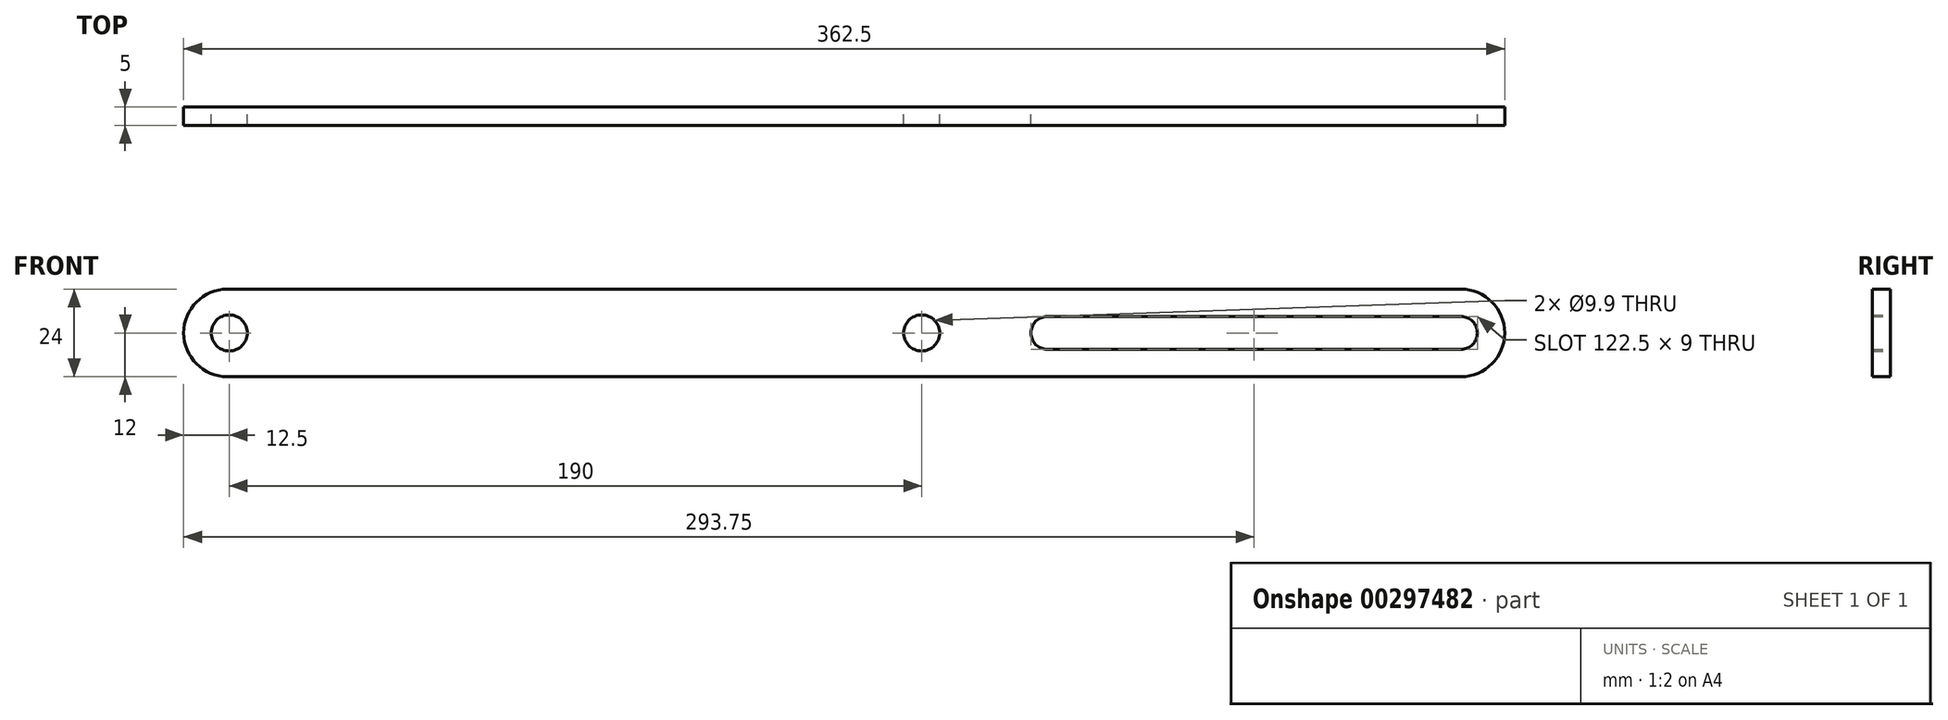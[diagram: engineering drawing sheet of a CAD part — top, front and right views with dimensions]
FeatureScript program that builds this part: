
annotation { "Feature Type Name" : "Feature", "Feature Type Description" : "" }
export const myFeature = defineFeature(function(context is Context, id is Id, definition is map)
    precondition{}
    {
        {
            var Q0;
            Q0=qCreatedBy(makeId("Front.planeOp"),FACE);
            var sketch = newSketch(context, id + "F0", { "sketchPlane" : qUnion([Q0])});
            skLineSegment(sketch, "E0.bottom", {"start": v(118, -12) * mm, "end": v(-220.5, -12) * mm});
            skLineSegment(sketch, "E0.top", {"start": v(118, 12) * mm, "end": v(-220.5, 12) * mm});
            skLineSegment(sketch, "E0.left", {"start": v(130, 0) * mm, "end": v(130, 0) * mm});
            skLineSegment(sketch, "E0.right", {"start": v(-232.5, 0) * mm, "end": v(-232.5, 0) * mm});
            skPoint(sketch, "E0.middle", {"position": v(0, 0) * mm});
            skCircle(sketch, "E1", {"center": v(-220, 0) * mm, "radius": 4.95 * mm});
            skLineSegment(sketch, "E2.bottom", {"start": v(118, -4.5) * mm, "end": v(4.5, -4.5) * mm});
            skLineSegment(sketch, "E2.top", {"start": v(118, 4.5) * mm, "end": v(4.5, 4.5) * mm});
            skLineSegment(sketch, "E2.left", {"start": v(122.5, 0) * mm, "end": v(122.5, 0) * mm});
            skLineSegment(sketch, "E2.right", {"start": v(0, 0) * mm, "end": v(0, 0) * mm});
            skPoint(sketch, "E2.middle", {"position": v(61.25, 0) * mm});
            skCircle(sketch, "E3", {"center": v(-30, 0) * mm, "radius": 4.95 * mm});
            skPoint(sketch, "E4.visualSharp", {"position": v(-232.5, 12) * mm});
            skArc(sketch, "E4.filletArc", {"start": v(-220.5, 12) * mm, "mid": v(-228.99, 8.49) * mm, "end": v(-232.5, 0) * mm});
            skPoint(sketch, "E5.visualSharp", {"position": v(-232.5, -12) * mm});
            skArc(sketch, "E5.filletArc", {"start": v(-232.5, 0) * mm, "mid": v(-228.99, -8.49) * mm, "end": v(-220.5, -12) * mm});
            skPoint(sketch, "E6.visualSharp", {"position": v(130, 12) * mm});
            skArc(sketch, "E6.filletArc", {"start": v(130, 0) * mm, "mid": v(126.49, 8.49) * mm, "end": v(118, 12) * mm});
            skPoint(sketch, "E7.visualSharp", {"position": v(130, -12) * mm});
            skArc(sketch, "E7.filletArc", {"start": v(118, -12) * mm, "mid": v(126.49, -8.49) * mm, "end": v(130, 0) * mm});
            skPoint(sketch, "E8.visualSharp", {"position": v(122.5, 4.5) * mm});
            skPoint(sketch, "E9.visualSharp", {"position": v(122.5, -4.5) * mm});
            skPoint(sketch, "E10.visualSharp", {"position": v(0, 4.5) * mm});
            skPoint(sketch, "E11.visualSharp", {"position": v(0, -4.5) * mm});
            skArc(sketch, "E12.filletArc", {"start": v(4.5, 4.5) * mm, "mid": v(1.32, 3.18) * mm, "end": v(0, 0) * mm});
            skArc(sketch, "E13.filletArc", {"start": v(0, 0) * mm, "mid": v(1.32, -3.18) * mm, "end": v(4.5, -4.5) * mm});
            skArc(sketch, "E14.filletArc", {"start": v(122.5, 0) * mm, "mid": v(121.18, 3.18) * mm, "end": v(118, 4.5) * mm});
            skArc(sketch, "E15.filletArc", {"start": v(118, -4.5) * mm, "mid": v(121.18, -3.18) * mm, "end": v(122.5, 0) * mm});
            skSolve(sketch);
        }
        {
            var Q0;
            Q0=makeQuery(id+"F0.imprint","IMPRINT",FACE,{"disambiguationData":[TD([[makeQuery(id+"F0.imprint","IMPRINT",EDGE,{"derivedFrom":sQuery(id+"F0.wireOp",EDGE,"E0.bottom")}),-1.0]])]});
            extrude(context, id + "F1", {"entities" : qUnion([Q0]), "depth" : 5 * mm});
        }
    });
